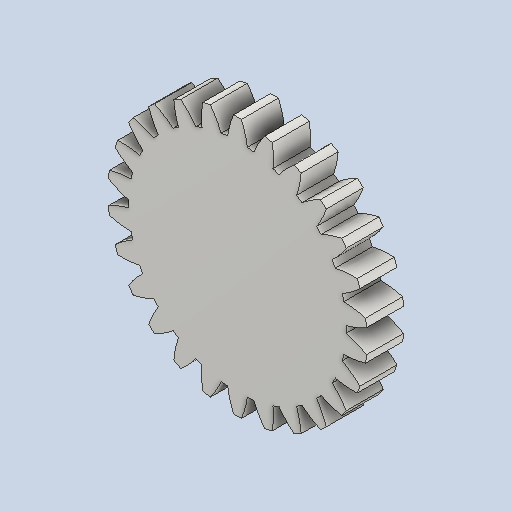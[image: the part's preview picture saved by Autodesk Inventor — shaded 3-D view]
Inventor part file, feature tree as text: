
AUTODESK INVENTOR PART (.ipt)
format: ipt  version: 2024 (Build 280153000, 153)  size: 253,440 bytes
history: native  units: mm (DEFAULTED — no unit token found)
features: plane x3, other x3, extrude x1, sketch x1
ambient origin geometry x8: Origin, YZ Plane, XZ Plane, XY Plane, X Axis, Y Axis, Z Axis, Center Point
bodies: Solid1 (feature_tree)
feature tree (8):
  extrude  "Extrusion1"  Depth=20.0mm TaperAngle=0.0deg
  plane  "Work Plane2"
  plane  "Work Plane8"
  plane  "Work Plane9"
  other  "Spur Gear"
  sketch  "Sketch1"  dims[d0=140.0mm d1=20.0mm d2=0.0mm d3=130.0mm d4=10.0mm d5=0.0mm d16=140.0mm d17=0.0mm d34=1.208305mm d39=0.0mm d41=0.0mm d43=140.0mm d46=140.0mm d47=0.0mm d48=0.0mm]
  other  "Srf1"
  other  "Pitch Diameter"
